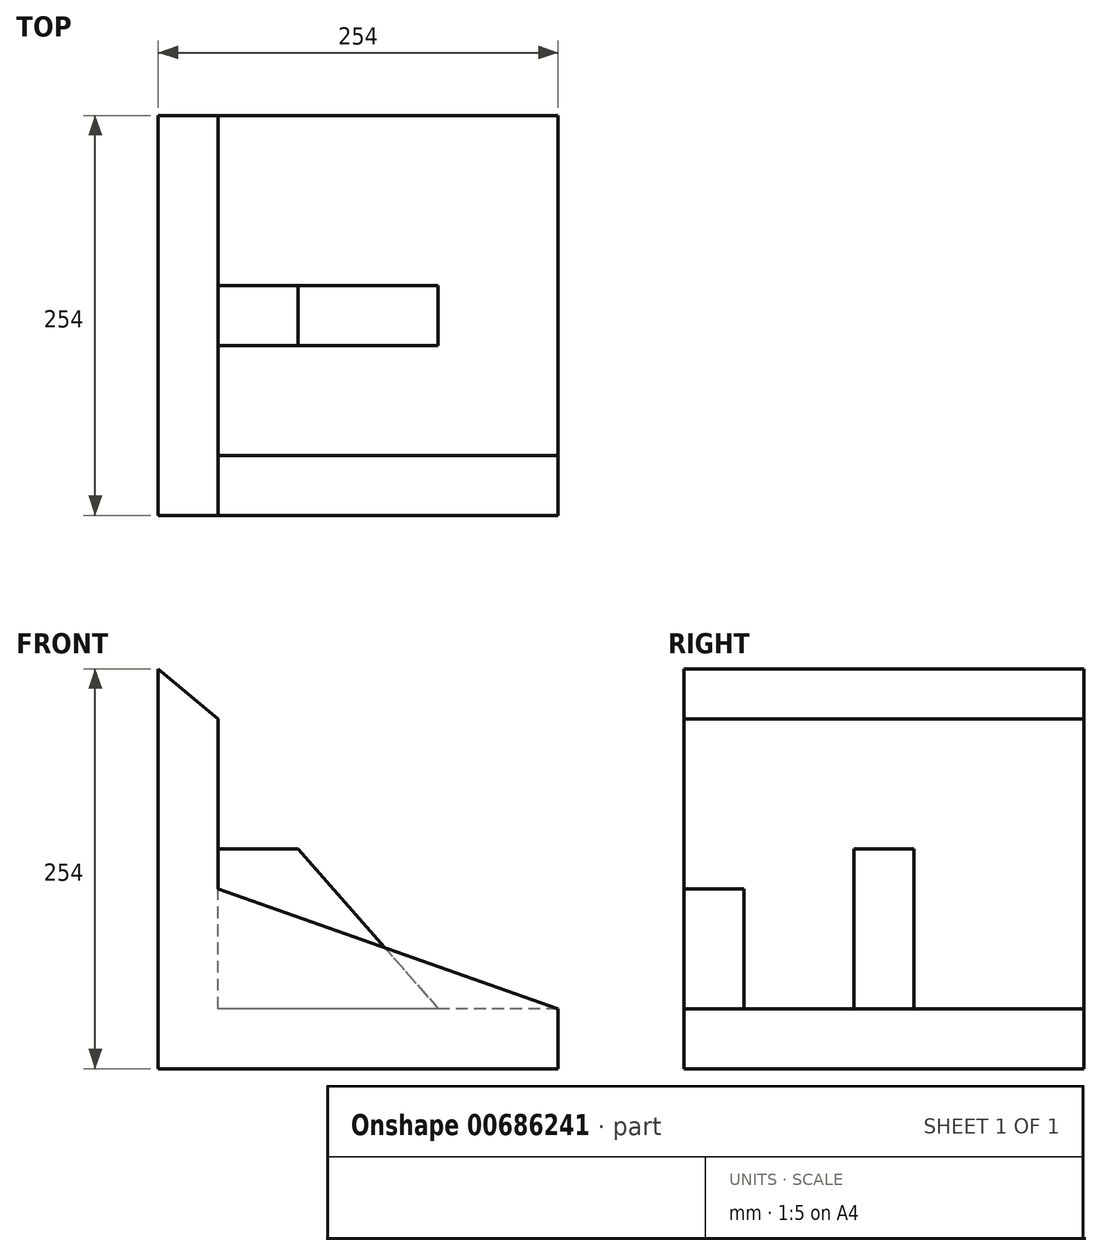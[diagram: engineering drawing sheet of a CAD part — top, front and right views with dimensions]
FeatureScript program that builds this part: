
annotation { "Feature Type Name" : "Feature", "Feature Type Description" : "" }
export const myFeature = defineFeature(function(context is Context, id is Id, definition is map)
    precondition{}
    {
        {
            var Q0;
            Q0=qCreatedBy(makeId("Front.planeOp"),FACE);
            var sketch = newSketch(context, id + "F0", { "sketchPlane" : qUnion([Q0])});
            skLineSegment(sketch, "E0", {"start": v(0, 0) * mm, "end": v(254, 0) * mm});
            skLineSegment(sketch, "E1", {"start": v(0, 0) * mm, "end": v(0, 254) * mm});
            skLineSegment(sketch, "E2", {"start": v(254, 0) * mm, "end": v(254, 38.1) * mm});
            skLineSegment(sketch, "E3", {"start": v(254, 38.1) * mm, "end": v(38.1, 38.1) * mm});
            skLineSegment(sketch, "E4", {"start": v(38.1, 38.1) * mm, "end": v(38.1, 222.25) * mm});
            skLineSegment(sketch, "E5", {"start": v(38.1, 222.25) * mm, "end": v(0, 254) * mm});
            skLineSegment(sketch, "E6", {"start": v(38.1, 139.7) * mm, "end": v(88.9, 139.7) * mm});
            skLineSegment(sketch, "E7", {"start": v(88.9, 139.7) * mm, "end": v(177.8, 38.1) * mm});
            skSolve(sketch);
        }
        {
            var Q0;
            Q0=makeQuery(id+"F0.imprint","IMPRINT",FACE,{"disambiguationData":[TD([[makeQuery(id+"F0.imprint","IMPRINT",EDGE,{"derivedFrom":sQuery(id+"F0.wireOp",EDGE,"E0")}),1.0]])]});
            extrude(context, id + "F1", {"entities" : qUnion([Q0]), "endBound" : BoundingType.SYMMETRIC, "depth" : 254 * mm, "offsetDistance" : 25.4 * mm});
        }
        {
            var Q0;
            {var subQ4=sQuery(id+"F0.wireOp",EDGE,"E6");Q0=makeQuery(id+"F0.imprint","IMPRINT",FACE,{"disambiguationData":[TD([[makeQuery(id+"F0.imprint","IMPRINT",EDGE,{"derivedFrom":subQ4}),-1.0]])]});}
            extrude(context, id + "F2", {"entities" : qUnion([Q0]), "operationType" : NewBodyOperationType.ADD, "endBound" : BoundingType.SYMMETRIC, "depth" : 38.1 * mm, "offsetDistance" : 25.4 * mm});
        }
        {
            var Q0;
            Q0=makeQuery(id+"F1.opExtrude","CAP_FACE",FACE,{"disambiguationData":[OSD([sQuery(id+"F0.wireOp",EDGE,"E0"),sQuery(id+"F0.wireOp",EDGE,"E1"),sQuery(id+"F0.wireOp",EDGE,"E2"),sQuery(id+"F0.wireOp",EDGE,"E3"),sQuery(id+"F0.wireOp",EDGE,"E4"),sQuery(id+"F0.wireOp",EDGE,"E5")])],"isStart":false});
            var sketch = newSketch(context, id + "F3", { "sketchPlane" : qUnion([Q0])});
            skLineSegment(sketch, "E8", {"start": v(38.1, 114.3) * mm, "end": v(254, 38.1) * mm});
            skSolve(sketch);
        }
        {
            var Q0;
            {var subQ0=sQuery(id+"F3.wireOp",EDGE,"E8");Q0=makeQuery(id+"F3.imprint","IMPRINT",FACE,{"disambiguationData":[TD([[makeQuery(id+"F3.imprint","IMPRINT",EDGE,{"derivedFrom":subQ0}),-1.0]])]});}
            extrude(context, id + "F4", {"entities" : qUnion([Q0]), "operationType" : NewBodyOperationType.ADD, "oppositeDirection" : true, "depth" : 38.1 * mm, "offsetDistance" : 25.4 * mm});
        }
    });
